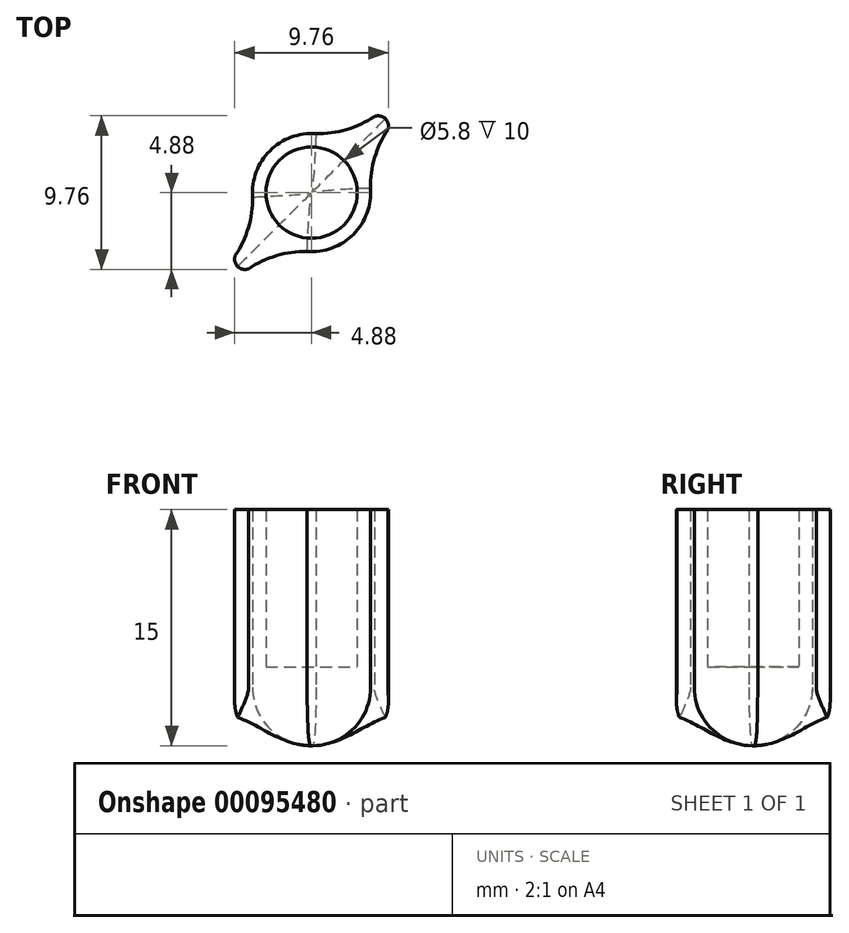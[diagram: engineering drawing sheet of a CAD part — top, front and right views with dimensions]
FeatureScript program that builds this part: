
annotation { "Feature Type Name" : "Feature", "Feature Type Description" : "" }
export const myFeature = defineFeature(function(context is Context, id is Id, definition is map)
    precondition{}
    {
        {
            var Q0;
            Q0=qCreatedBy(makeId("Top.planeOp"),FACE);
            var sketch = newSketch(context, id + "F0", { "sketchPlane" : qUnion([Q0])});
            skCircle(sketch, "E0", {"center": v(0, 0) * mm, "radius": 2.9 * mm});
            skCircle(sketch, "E1", {"center": v(0, 0) * mm, "radius": 3.75 * mm});
            skLineSegment(sketch, "E2", {"start": v(-2.65, -2.65) * mm, "end": v(2.65, 2.65) * mm});
            skLineSegment(sketch, "E3", {"start": v(2.65, 2.65) * mm, "end": v(4.42, 4.42) * mm});
            skLineSegment(sketch, "E4", {"start": v(-2.65, -2.65) * mm, "end": v(-4.42, -4.42) * mm});
            skLineSegment(sketch, "E5", {"start": v(4.42, 4.42) * mm, "end": v(4.84, 4) * mm});
            skLineSegment(sketch, "E6.MirrorCS", {"start": v(4.42, 4.42) * mm, "end": v(4, 4.84) * mm});
            skArc(sketch, "E7", {"start": v(4.84, 4) * mm, "mid": v(3.97, 2.09) * mm, "end": v(3.75, 0) * mm});
            skArc(sketch, "E8", {"start": v(4.84, 4) * mm, "mid": v(4.87, 4.36) * mm, "end": v(4.69, 4.69) * mm});
            skPoint(sketch, "E9", {"position": v(4.69, 4.69) * mm});
            skArc(sketch, "E10.MirrorCS", {"start": v(4, 4.84) * mm, "mid": v(2.09, 3.97) * mm, "end": v(0, 3.75) * mm});
            skArc(sketch, "E11.MirrorCS", {"start": v(4, 4.84) * mm, "mid": v(4.36, 4.87) * mm, "end": v(4.69, 4.69) * mm});
            skLineSegment(sketch, "E12", {"start": v(0, 0) * mm, "end": v(1.28, -1.28) * mm});
            skArc(sketch, "E13.MirrorCS", {"start": v(-4, -4.84) * mm, "mid": v(-4.36, -4.87) * mm, "end": v(-4.69, -4.69) * mm});
            skArc(sketch, "E14.MirrorCS", {"start": v(-4.84, -4) * mm, "mid": v(-4.87, -4.36) * mm, "end": v(-4.69, -4.69) * mm});
            skArc(sketch, "E15.MirrorCS", {"start": v(-4.84, -4) * mm, "mid": v(-3.97, -2.09) * mm, "end": v(-3.75, 0) * mm});
            skArc(sketch, "E16.MirrorCS", {"start": v(-4, -4.84) * mm, "mid": v(-2.09, -3.97) * mm, "end": v(0, -3.75) * mm});
            skSolve(sketch);
        }
        {
            var Q0;
            Q0 = qSketchRegion(id + "F0", true);
            extrude(context, id + "F1", {"entities" : qUnion([Q0]), "depth" : 15 * mm});
        }
        {
            var Q0;
            Q0=makeQuery(id+"F1.opExtrude","CAP_FACE",FACE,{"disambiguationData":[OSD([sQuery(id+"F0.wireOp",EDGE,"E0"),sQuery(id+"F0.wireOp",EDGE,"E1"),sQuery(id+"F0.wireOp",EDGE,"E7"),sQuery(id+"F0.wireOp",EDGE,"E8"),sQuery(id+"F0.wireOp",EDGE,"E10.MirrorCS"),sQuery(id+"F0.wireOp",EDGE,"E11.MirrorCS"),sQuery(id+"F0.wireOp",EDGE,"E13.MirrorCS"),sQuery(id+"F0.wireOp",EDGE,"E14.MirrorCS"),sQuery(id+"F0.wireOp",EDGE,"E15.MirrorCS"),sQuery(id+"F0.wireOp",EDGE,"E16.MirrorCS")])],"isStart":true});
            var sketch = newSketch(context, id + "F2", { "sketchPlane" : qUnion([Q0])});
            skCircle(sketch, "E17", {"center": v(0, 0) * mm, "radius": 2.94 * mm});
            skSolve(sketch);
        }
        {
            var Q0;
            Q0 = qSketchRegion(id + "F2", true);
            extrude(context, id + "F3", {"entities" : qUnion([Q0]), "operationType" : NewBodyOperationType.ADD, "oppositeDirection" : true, "depth" : 5 * mm});
        }
        {
            var Q0;
            {var subQ0=sQuery(id+"F0.wireOp",EDGE,"E15.MirrorCS");var subQ1=sQuery(id+"F0.wireOp",EDGE,"E1");var subQ2=makeQuery(id+"F0.imprint","INTERSECT",VERTEX,{"disambiguationData":[OD(0.0)],"derivedFrom":[subQ1,subQ0]});var subQ3=sQuery(id+"F0.wireOp",EDGE,"E10.MirrorCS");var subQ4=makeQuery(id+"F0.imprint","INTERSECT",VERTEX,{"disambiguationData":[OD(0.0)],"derivedFrom":[subQ1,subQ3]});Q0=makeQuery(id+"F1.opExtrude","CAP_EDGE",EDGE,{"disambiguationData":[OSD([subQ1]),TDD([makeQuery(id+"F0.imprint","IMPRINT",EDGE,{"disambiguationData":[TD([[subQ4,1.0]])],"derivedFrom":subQ1}),makeQuery(id+"F0.imprint","IMPRINT",EDGE,{"disambiguationData":[TD([[subQ4,-1.0]])],"derivedFrom":subQ1}),makeQuery(id+"F0.imprint","IMPRINT",EDGE,{"disambiguationData":[TD([[subQ2,-1.0]])],"derivedFrom":subQ1})])],"isStart":true});}
            var Q1;
            {var subQ0=sQuery(id+"F0.wireOp",EDGE,"E7");var subQ1=sQuery(id+"F0.wireOp",EDGE,"E1");var subQ2=makeQuery(id+"F0.imprint","INTERSECT",VERTEX,{"disambiguationData":[OD(0.0)],"derivedFrom":[subQ1,subQ0]});var subQ3=sQuery(id+"F0.wireOp",EDGE,"E16.MirrorCS");var subQ4=makeQuery(id+"F0.imprint","INTERSECT",VERTEX,{"disambiguationData":[OD(0.0)],"derivedFrom":[subQ1,subQ3]});Q1=makeQuery(id+"F1.opExtrude","CAP_EDGE",EDGE,{"disambiguationData":[OSD([subQ1]),TDD([makeQuery(id+"F0.imprint","IMPRINT",EDGE,{"disambiguationData":[TD([[subQ2,-1.0]])],"derivedFrom":subQ1}),makeQuery(id+"F0.imprint","IMPRINT",EDGE,{"disambiguationData":[TD([[subQ4,1.0]])],"derivedFrom":subQ1}),makeQuery(id+"F0.imprint","IMPRINT",EDGE,{"disambiguationData":[TD([[subQ2,1.0]])],"derivedFrom":subQ1})])],"isStart":true});}
            fillet(context, id + "F4", {"entities" : qUnion([Q0, Q1]), "radius" : 3.7 * mm, "tangentPropagation" : true, "allowEdgeOverflow" : false});
        }
    });
